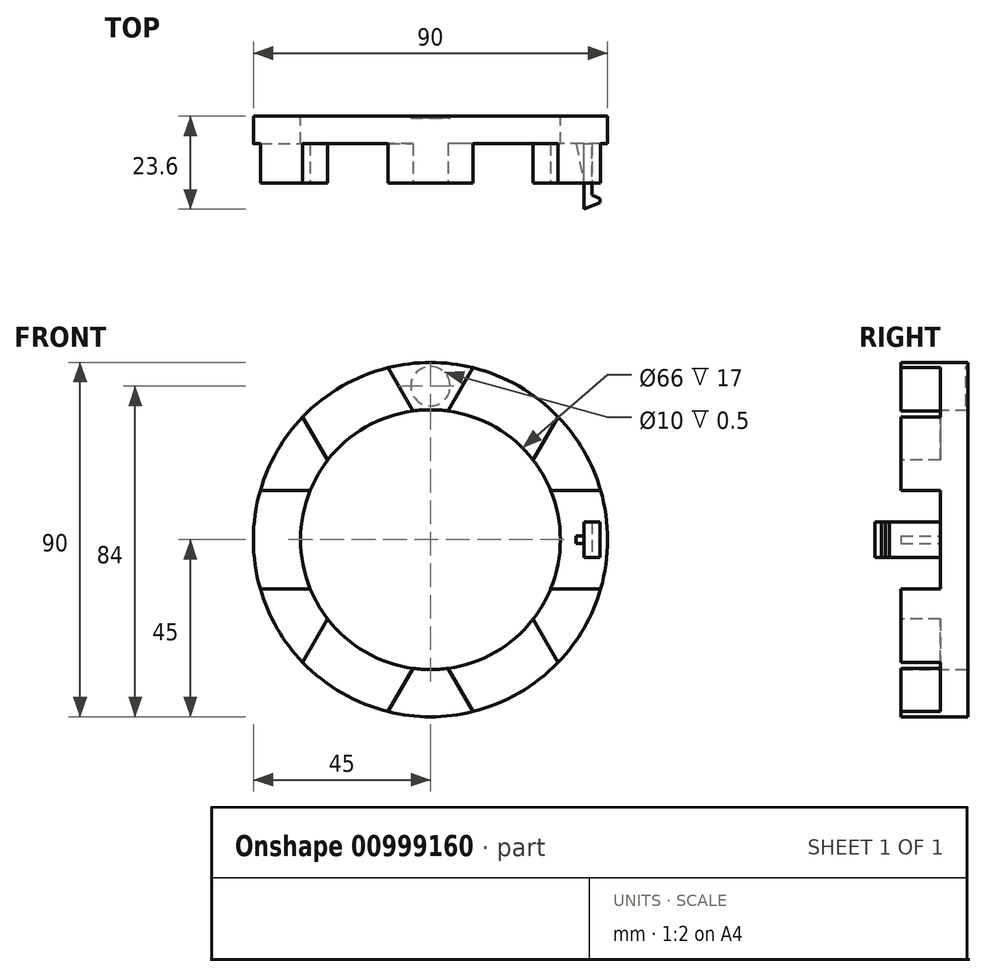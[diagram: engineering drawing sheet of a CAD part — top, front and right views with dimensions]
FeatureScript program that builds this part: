
annotation { "Feature Type Name" : "Feature", "Feature Type Description" : "" }
export const myFeature = defineFeature(function(context is Context, id is Id, definition is map)
    precondition{}
    {
        {
            var Q0;
            Q0=qCreatedBy(makeId("Front.planeOp"),FACE);
            var sketch = newSketch(context, id + "F0", { "sketchPlane" : qUnion([Q0])});
            skCircle(sketch, "E0", {"center": v(0, 0) * mm, "radius": 45 * mm});
            skLineSegment(sketch, "E1", {"start": v(0, 0) * mm, "end": v(0, 33) * mm, "construction": true});
            skCircle(sketch, "E2", {"center": v(0, 0) * mm, "radius": 33 * mm});
            skSolve(sketch);
        }
        {
            var Q0;
            Q0=makeQuery(id+"F0.imprint","IMPRINT",FACE,{"disambiguationData":[TD([[makeQuery(id+"F0.imprint","IMPRINT",EDGE,{"derivedFrom":sQuery(id+"F0.wireOp",EDGE,"E0")}),1.0]])]});
            extrude(context, id + "F1", {"entities" : qUnion([Q0]), "depth" : 17 * mm, "offsetDistance" : 25 * mm});
        }
        {
            var Q0;
            Q0=qCreatedBy(makeId("Front.planeOp"),FACE);
            var sketch = newSketch(context, id + "F2", { "sketchPlane" : qUnion([Q0])});
            skLineSegment(sketch, "E3", {"start": v(0, 0) * mm, "end": v(0, 39) * mm, "construction": true});
            skCircle(sketch, "E4", {"center": v(0, 39) * mm, "radius": 5 * mm});
            skSolve(sketch);
        }
        {
            var Q0;
            Q0=makeQuery(id+"F2.imprint","IMPRINT",FACE,{"disambiguationData":[TD([[makeQuery(id+"F2.imprint","IMPRINT",EDGE,{"derivedFrom":sQuery(id+"F2.wireOp",EDGE,"E4")}),1.0]])]});
            extrude(context, id + "F3", {"entities" : qUnion([Q0]), "operationType" : NewBodyOperationType.REMOVE, "depth" : 0.5 * mm, "offsetDistance" : 25 * mm});
        }
        {
            var Q0;
            Q0=qCreatedBy(makeId("Top.planeOp"),FACE);
            var sketch = newSketch(context, id + "F4", { "sketchPlane" : qUnion([Q0])});
            skLineSegment(sketch, "E5", {"start": v(0, 0) * mm, "end": v(0, -30.02) * mm, "construction": true});
            skSolve(sketch);
        }
        {
            var Q0;
            Q0=makeQuery(id+"F1.opExtrude","CAP_FACE",FACE,{"disambiguationData":[OSD([sQuery(id+"F0.wireOp",EDGE,"E0"),sQuery(id+"F0.wireOp",EDGE,"E2")])],"isStart":false});
            var sketch = newSketch(context, id + "F5", { "sketchPlane" : qUnion([Q0])});
            skLineSegment(sketch, "E6.bottom", {"start": v(-50.5, 12.5) * mm, "end": v(-15.5, 12.5) * mm});
            skLineSegment(sketch, "E6.top", {"start": v(-50.5, -12.5) * mm, "end": v(-15.5, -12.5) * mm});
            skLineSegment(sketch, "E6.left", {"start": v(-50.5, 12.5) * mm, "end": v(-50.5, -12.5) * mm});
            skLineSegment(sketch, "E6.right", {"start": v(-15.5, 12.5) * mm, "end": v(-15.5, -12.5) * mm});
            skPoint(sketch, "E6.middle", {"position": v(-33, 0) * mm});
            skSolve(sketch);
        }
        {
            var Q0;
            {var subQ0=sQuery(id+"F5.wireOp",EDGE,"E6.bottom");var subQ1=makeQuery(id+"F1.opExtrude","CAP_EDGE",EDGE,{"disambiguationData":[OSD([sQuery(id+"F0.wireOp",EDGE,"E0")])],"isStart":false});var subQ2=makeQuery(id+"F5.imprint","INTERSECT",VERTEX,{"derivedFrom":[subQ1,subQ0]});Q0=makeQuery(id+"F5.imprint","IMPRINT",FACE,{"disambiguationData":[TD([[makeQuery(id+"F5.imprint","IMPRINT",EDGE,{"disambiguationData":[TD([[subQ2,-1.0]])],"derivedFrom":subQ0}),-1.0]])]});}
            extrude(context, id + "F6", {"entities" : qUnion([Q0]), "operationType" : NewBodyOperationType.REMOVE, "oppositeDirection" : true, "depth" : 10 * mm, "offsetDistance" : 25 * mm});
        }
        {
            var Q0;
            Q0=qCreatedBy(makeId("Top.planeOp"),FACE);
            var sketch = newSketch(context, id + "F7", { "sketchPlane" : qUnion([Q0])});
            skLineSegment(sketch, "E7", {"start": v(0, 0) * mm, "end": v(0, -40.23) * mm, "construction": true});
            skSolve(sketch);
        }
        {
            var Q0;
            Q0=makeQuery(id+"F6.boolean.opBoolean","COPY",FACE,{"derivedFrom":makeQuery(id+"F6.opExtrude","SWEPT_FACE",FACE,{"disambiguationData":[OSD([sQuery(id+"F5.wireOp",EDGE,"E6.bottom")])]})});
            var Q1;
            Q1=makeQuery(id+"F6.boolean.opBoolean","COPY",FACE,{"derivedFrom":makeQuery(id+"F6.opExtrude","CAP_FACE",FACE,{"disambiguationData":[OSD([sQuery(id+"F0.wireOp",EDGE,"E0"),sQuery(id+"F0.wireOp",EDGE,"E2"),sQuery(id+"F5.wireOp",EDGE,"E6.bottom"),sQuery(id+"F5.wireOp",EDGE,"E6.top")])],"isStart":false})});
            var Q2;
            Q2=makeQuery(id+"F6.boolean.opBoolean","COPY",FACE,{"derivedFrom":makeQuery(id+"F6.opExtrude","SWEPT_FACE",FACE,{"disambiguationData":[OSD([sQuery(id+"F5.wireOp",EDGE,"E6.top")])]})});
            var Q3;
            Q3=sQuery(id+"F7.wireOp",EDGE,"E7");
            circularPattern(context, id + "F8", {"patternType" : PatternType.FACE, "faces" : qUnion([Q0, Q1, Q2]), "axis" : qUnion([Q3]), "angle" : 360 * degree, "instanceCount" : 6, "equalSpace" : true});
        }
        {
            var Q0;
            Q0=makeQuery(id+"F6.boolean.opBoolean","COPY",FACE,{"derivedFrom":makeQuery(id+"F6.opExtrude","CAP_FACE",FACE,{"disambiguationData":[OSD([sQuery(id+"F0.wireOp",EDGE,"E0"),sQuery(id+"F0.wireOp",EDGE,"E2"),sQuery(id+"F5.wireOp",EDGE,"E6.bottom"),sQuery(id+"F5.wireOp",EDGE,"E6.top")])],"isStart":false})});
            var sketch = newSketch(context, id + "F9", { "sketchPlane" : qUnion([Q0])});
            skPoint(sketch, "E8.startSnap0", {"position": v(-33, 0) * mm});
            skLineSegment(sketch, "E9", {"start": v(-45, 0) * mm, "end": v(45, 0) * mm, "construction": true});
            skLineSegment(sketch, "E10", {"start": v(0, 0) * mm, "end": v(42, 0) * mm, "construction": true});
            skLineSegment(sketch, "E11.bottom", {"start": v(39, 4.5) * mm, "end": v(45, 4.5) * mm});
            skLineSegment(sketch, "E11.top", {"start": v(39, -4.5) * mm, "end": v(45, -4.5) * mm});
            skLineSegment(sketch, "E11.left", {"start": v(39, 4.5) * mm, "end": v(39, -4.5) * mm});
            skLineSegment(sketch, "E11.right", {"start": v(45, 4.5) * mm, "end": v(45, -4.5) * mm});
            skPoint(sketch, "E11.middle", {"position": v(42, 0) * mm});
            skSolve(sketch);
        }
        {
            var Q0;
            Q0=makeQuery(id+"F9.imprint","IMPRINT",FACE,{"disambiguationData":[TD([[makeQuery(id+"F9.imprint","IMPRINT",EDGE,{"derivedFrom":sQuery(id+"F9.wireOp",EDGE,"E11.bottom")}),-1.0]])]});
            extrude(context, id + "F10", {"entities" : qUnion([Q0]), "operationType" : NewBodyOperationType.ADD, "depth" : 17 * mm, "offsetDistance" : 25 * mm});
        }
        {
            var Q0;
            Q0=makeQuery(id+"F10.opExtrude","SWEPT_FACE",FACE,{"disambiguationData":[OSD([sQuery(id+"F9.wireOp",EDGE,"E11.top")])]});
            var sketch = newSketch(context, id + "F11", { "sketchPlane" : qUnion([Q0])});
            skLineSegment(sketch, "E12", {"start": v(38, 24) * mm, "end": v(43, 22) * mm});
            skLineSegment(sketch, "E13", {"start": v(43, 22) * mm, "end": v(43, 21) * mm});
            skLineSegment(sketch, "E14", {"start": v(43, 21) * mm, "end": v(41, 20) * mm});
            skLineSegment(sketch, "E15", {"start": v(41, 20) * mm, "end": v(41, 7) * mm});
            skSolve(sketch);
        }
        {
            var Q0;
            {var subQ1=sQuery(id+"F11.wireOp",EDGE,"rFHcq0DC-XCo2-NJZE-bYMH-Lx2zlDmxOu08");Q0=makeQuery(id+"F11.imprint","IMPRINT",FACE,{"disambiguationData":[TD([[makeQuery(id+"F11.imprint","IMPRINT",EDGE,{"derivedFrom":subQ1}),-1.0]])]});}
            var Q1;
            {var subQ1=sQuery(id+"F11.wireOp",EDGE,"E12");Q1=makeQuery(id+"F11.imprint","IMPRINT",FACE,{"disambiguationData":[TD([[makeQuery(id+"F11.imprint","IMPRINT",EDGE,{"derivedFrom":subQ1}),1.0]])]});}
            extrude(context, id + "F12", {"entities" : qUnion([Q0, Q1]), "operationType" : NewBodyOperationType.REMOVE, "oppositeDirection" : true, "depth" : 10 * mm, "offsetDistance" : 25 * mm});
        }
        {
            var Q0;
            Q0=qCreatedBy(makeId("Top.planeOp"),FACE);
            var sketch = newSketch(context, id + "F13", { "sketchPlane" : qUnion([Q0])});
            skLineSegment(sketch, "E16", {"start": v(39, -17) * mm, "end": v(39, -7) * mm});
            skLineSegment(sketch, "E17", {"start": v(39, -7) * mm, "end": v(37, -7) * mm});
            skLineSegment(sketch, "E18", {"start": v(37, -7) * mm, "end": v(39, -17) * mm});
            skSolve(sketch);
        }
        {
            var Q0;
            Q0=makeQuery(id+"F13.imprint","IMPRINT",FACE,{"disambiguationData":[TD([[makeQuery(id+"F13.imprint","IMPRINT",EDGE,{"derivedFrom":sQuery(id+"F13.wireOp",EDGE,"E16")}),1.0]])]});
            extrude(context, id + "F14", {"entities" : qUnion([Q0]), "operationType" : NewBodyOperationType.ADD, "endBound" : BoundingType.SYMMETRIC, "depth" : 2 * mm, "offsetDistance" : 25 * mm});
        }
    });
